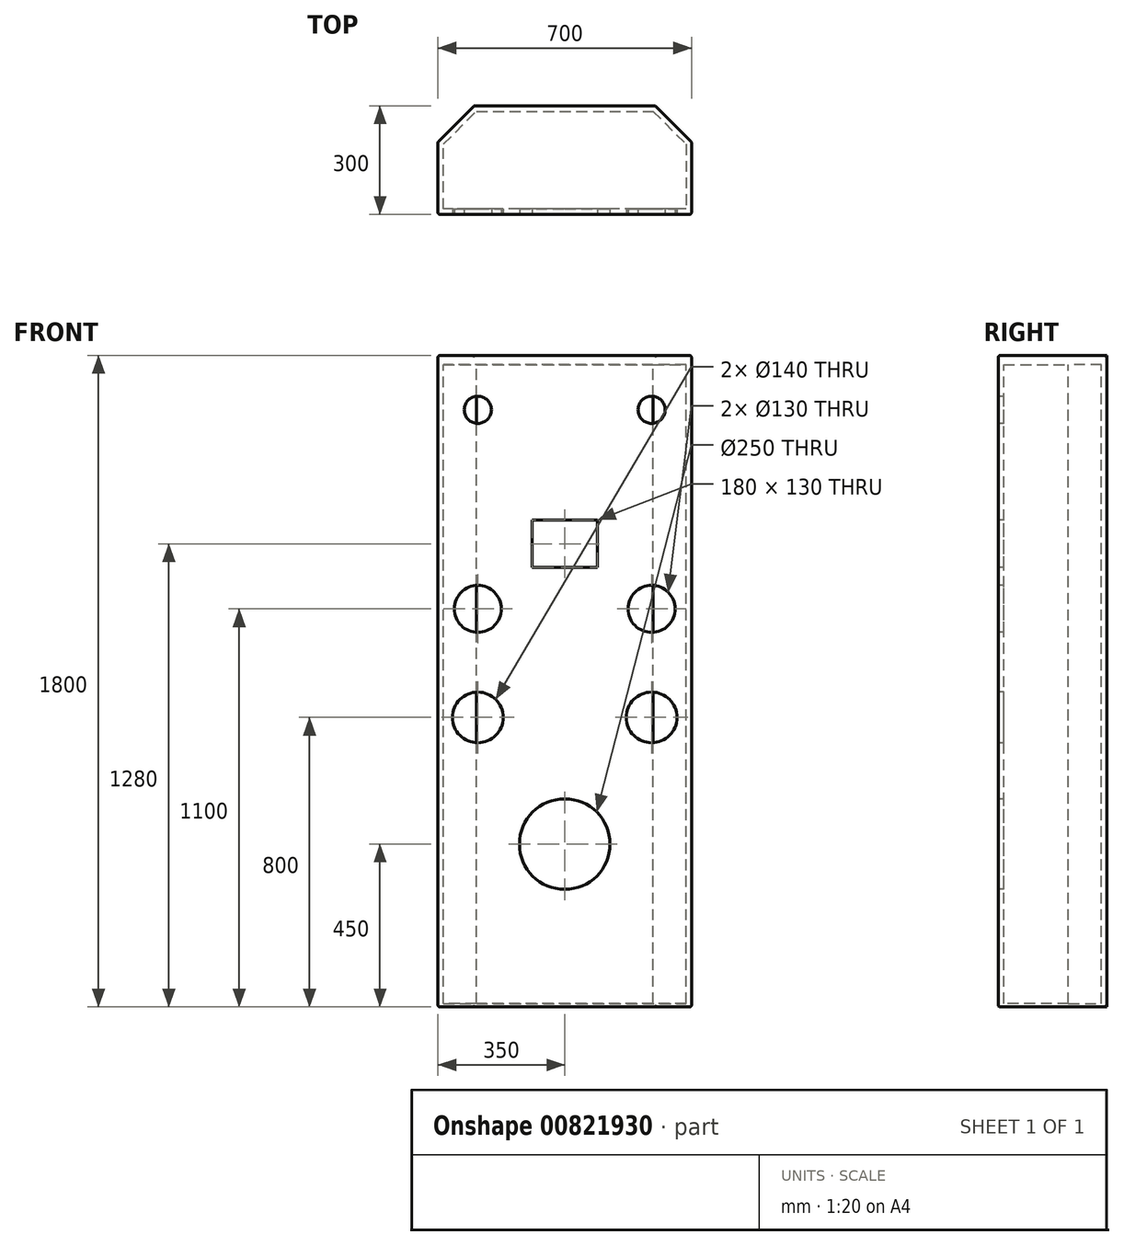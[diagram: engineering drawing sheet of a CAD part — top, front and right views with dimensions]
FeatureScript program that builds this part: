
annotation { "Feature Type Name" : "Feature", "Feature Type Description" : "" }
export const myFeature = defineFeature(function(context is Context, id is Id, definition is map)
    precondition{}
    {
        {
            var Q0;
            Q0=qCreatedBy(makeId("Top.planeOp"),FACE);
            var sketch = newSketch(context, id + "F0", { "sketchPlane" : qUnion([Q0])});
            skLineSegment(sketch, "E0.bottom", {"start": v(350, -150) * mm, "end": v(-350, -150) * mm});
            skLineSegment(sketch, "E0.top", {"start": v(250, 150) * mm, "end": v(-250, 150) * mm});
            skLineSegment(sketch, "E0.left", {"start": v(350, -150) * mm, "end": v(350, 50) * mm});
            skLineSegment(sketch, "E0.right", {"start": v(-350, -150) * mm, "end": v(-350, 50) * mm});
            skPoint(sketch, "E0.middle", {"position": v(0, 0) * mm});
            skLineSegment(sketch, "E1", {"start": v(0, 150) * mm, "end": v(-250, 150) * mm});
            skLineSegment(sketch, "E2", {"start": v(-350, 50) * mm, "end": v(-250, 150) * mm});
            skLineSegment(sketch, "E3", {"start": v(0, 150) * mm, "end": v(250, 150) * mm});
            skLineSegment(sketch, "E4", {"start": v(350, 50) * mm, "end": v(250, 150) * mm});
            skPoint(sketch, "E5.orphan", {"position": v(-350, 150) * mm});
            skPoint(sketch, "E6.orphan", {"position": v(350, 150) * mm});
            skSolve(sketch);
        }
        {
            var Q0;
            Q0 = qSketchRegion(id + "F0", true);
            extrude(context, id + "F1", {"entities" : qUnion([Q0]), "depth" : 1800 * mm, "offsetDistance" : 25 * mm});
        }
        {
            var Q0;
            Q0=makeQuery(id+"F1.opExtrude","SWEPT_EDGE",EDGE,{"disambiguationData":[OSD([sQuery(id+"F0.wireOp",EDGE,"E0.bottom"),sQuery(id+"F0.wireOp",EDGE,"E0.right")])]});
            var Q1;
            Q1=makeQuery(id+"F1.opExtrude","CAP_EDGE",EDGE,{"disambiguationData":[OSD([sQuery(id+"F0.wireOp",EDGE,"E0.bottom")])],"isStart":false});
            var Q2;
            Q2=makeQuery(id+"F1.opExtrude","SWEPT_EDGE",EDGE,{"disambiguationData":[OSD([sQuery(id+"F0.wireOp",EDGE,"E0.bottom"),sQuery(id+"F0.wireOp",EDGE,"E0.left")])]});
            var Q3;
            Q3=makeQuery(id+"F1.opExtrude","CAP_EDGE",EDGE,{"disambiguationData":[OSD([sQuery(id+"F0.wireOp",EDGE,"E0.bottom")])],"isStart":true});
            var Q4;
            Q4=makeQuery(id+"F1.opExtrude","CAP_EDGE",EDGE,{"disambiguationData":[OSD([sQuery(id+"F0.wireOp",EDGE,"E0.left")])],"isStart":true});
            var Q5;
            Q5=makeQuery(id+"F1.opExtrude","CAP_EDGE",EDGE,{"disambiguationData":[OSD([sQuery(id+"F0.wireOp",EDGE,"E0.right")])],"isStart":true});
            var Q6;
            Q6=makeQuery(id+"F1.opExtrude","CAP_EDGE",EDGE,{"disambiguationData":[OSD([sQuery(id+"F0.wireOp",EDGE,"E2")])],"isStart":true});
            var Q7;
            Q7=makeQuery(id+"F1.opExtrude","CAP_EDGE",EDGE,{"disambiguationData":[OSD([sQuery(id+"F0.wireOp",EDGE,"E1"),sQuery(id+"F0.wireOp",EDGE,"E3")])],"isStart":true});
            var Q8;
            Q8=makeQuery(id+"F1.opExtrude","CAP_EDGE",EDGE,{"disambiguationData":[OSD([sQuery(id+"F0.wireOp",EDGE,"E4")])],"isStart":true});
            var Q9;
            Q9=makeQuery(id+"F1.opExtrude","SWEPT_EDGE",EDGE,{"disambiguationData":[OSD([sQuery(id+"F0.wireOp",EDGE,"E0.left"),sQuery(id+"F0.wireOp",EDGE,"E4")])]});
            var Q10;
            Q10=makeQuery(id+"F1.opExtrude","SWEPT_EDGE",EDGE,{"disambiguationData":[OSD([sQuery(id+"F0.wireOp",EDGE,"E3"),sQuery(id+"F0.wireOp",EDGE,"E4")])]});
            var Q11;
            Q11=makeQuery(id+"F1.opExtrude","CAP_EDGE",EDGE,{"disambiguationData":[OSD([sQuery(id+"F0.wireOp",EDGE,"E4")])],"isStart":false});
            var Q12;
            Q12=makeQuery(id+"F1.opExtrude","CAP_EDGE",EDGE,{"disambiguationData":[OSD([sQuery(id+"F0.wireOp",EDGE,"E1"),sQuery(id+"F0.wireOp",EDGE,"E3")])],"isStart":false});
            var Q13;
            Q13=makeQuery(id+"F1.opExtrude","CAP_EDGE",EDGE,{"disambiguationData":[OSD([sQuery(id+"F0.wireOp",EDGE,"E0.left")])],"isStart":false});
            var Q14;
            Q14=makeQuery(id+"F1.opExtrude","CAP_EDGE",EDGE,{"disambiguationData":[OSD([sQuery(id+"F0.wireOp",EDGE,"E2")])],"isStart":false});
            var Q15;
            Q15=makeQuery(id+"F1.opExtrude","CAP_EDGE",EDGE,{"disambiguationData":[OSD([sQuery(id+"F0.wireOp",EDGE,"E0.right")])],"isStart":false});
            var Q16;
            Q16=makeQuery(id+"F1.opExtrude","SWEPT_EDGE",EDGE,{"disambiguationData":[OSD([sQuery(id+"F0.wireOp",EDGE,"E0.right"),sQuery(id+"F0.wireOp",EDGE,"E2")])]});
            var Q17;
            Q17=makeQuery(id+"F1.opExtrude","SWEPT_EDGE",EDGE,{"disambiguationData":[OSD([sQuery(id+"F0.wireOp",EDGE,"E1"),sQuery(id+"F0.wireOp",EDGE,"E2")])]});
            fillet(context, id + "F2", {"entities" : qUnion([Q0, Q1, Q2, Q3, Q4, Q5, Q6, Q7, Q8, Q9, Q10, Q11, Q12, Q13, Q14, Q15, Q16, Q17]), "radius" : 5 * mm, "tangentPropagation" : true, "allowEdgeOverflow" : false});
        }
        {
            var Q0;
            Q0=makeQuery(id+"F1.opExtrude","SWEPT_FACE",FACE,{"disambiguationData":[OSD([sQuery(id+"F0.wireOp",EDGE,"E0.bottom")])]});
            var sketch = newSketch(context, id + "F3", { "sketchPlane" : qUnion([Q0])});
            skLineSegment(sketch, "E7.bottom", {"start": v(-90, 1345) * mm, "end": v(90, 1345) * mm});
            skLineSegment(sketch, "E7.top", {"start": v(-90, 1215) * mm, "end": v(90, 1215) * mm});
            skLineSegment(sketch, "E7.left", {"start": v(-90, 1345) * mm, "end": v(-90, 1215) * mm});
            skLineSegment(sketch, "E7.right", {"start": v(90, 1345) * mm, "end": v(90, 1215) * mm});
            skLineSegment(sketch, "E8", {"start": v(0, 1795) * mm, "end": v(0, 5) * mm});
            skSolve(sketch);
        }
        {
            var Q0;
            Q0 = qSketchRegion(id + "F3", true);
            extrude(context, id + "F4", {"entities" : qUnion([Q0]), "operationType" : NewBodyOperationType.REMOVE, "oppositeDirection" : true, "depth" : 25 * mm, "offsetDistance" : 25 * mm});
        }
        {
            var Q0;
            Q0=makeQuery(id+"F1.opExtrude","CAP_FACE",FACE,{"disambiguationData":[OSD([sQuery(id+"F0.wireOp",EDGE,"E0.bottom"),sQuery(id+"F0.wireOp",EDGE,"E0.right"),sQuery(id+"F0.wireOp",EDGE,"E1"),sQuery(id+"F0.wireOp",EDGE,"E2"),sQuery(id+"F0.wireOp",EDGE,"E3"),sQuery(id+"F0.wireOp",EDGE,"E0.left"),sQuery(id+"F0.wireOp",EDGE,"E4")])],"isStart":false});
            var sketch = newSketch(context, id + "F5", { "sketchPlane" : qUnion([Q0])});
            skLineSegment(sketch, "E9.0", {"start": v(247.93, 145) * mm, "end": v(-247.93, 145) * mm});
            skLineSegment(sketch, "E10.0", {"start": v(243.79, 135) * mm, "end": v(-243.79, 135) * mm});
            skLineSegment(sketch, "E11.0", {"start": v(-243.79, 135) * mm, "end": v(-335, 43.79) * mm});
            skLineSegment(sketch, "E12.0", {"start": v(350, 50) * mm, "end": v(250, 150) * mm});
            skLineSegment(sketch, "E12.1", {"start": v(-250, 150) * mm, "end": v(-350, 50) * mm});
            skLineSegment(sketch, "E12.2", {"start": v(-350, 50) * mm, "end": v(-350, -150) * mm});
            skLineSegment(sketch, "E12.3", {"start": v(250, 150) * mm, "end": v(-250, 150) * mm});
            skLineSegment(sketch, "E12.4", {"start": v(-350, -150) * mm, "end": v(350, -150) * mm});
            skLineSegment(sketch, "E12.5", {"start": v(350, -150) * mm, "end": v(350, 50) * mm});
            skLineSegment(sketch, "E13.0", {"start": v(-335, 43.79) * mm, "end": v(-335, -135) * mm});
            skLineSegment(sketch, "E14.0", {"start": v(348.54, 51.46) * mm, "end": v(251.46, 148.54) * mm});
            skLineSegment(sketch, "E15.0", {"start": v(335, 43.79) * mm, "end": v(243.79, 135) * mm});
            skLineSegment(sketch, "E16.0", {"start": v(335, -135) * mm, "end": v(335, 43.79) * mm});
            skLineSegment(sketch, "E17.0", {"start": v(-335, -135) * mm, "end": v(335, -135) * mm});
            skSolve(sketch);
        }
        {
            var Q0;
            Q0=makeQuery(id+"F5.imprint","IMPRINT",FACE,{"disambiguationData":[TD([[makeQuery(id+"F5.imprint","IMPRINT",EDGE,{"derivedFrom":sQuery(id+"F5.wireOp",EDGE,"E10.0")}),1.0]])]});
            extrude(context, id + "F6", {"entities" : qUnion([Q0]), "operationType" : NewBodyOperationType.REMOVE, "oppositeDirection" : true, "depth" : 1790 * mm, "offsetDistance" : 25 * mm});
        }
        {
            var Q0;
            Q0=makeQuery(id+"F1.opExtrude","SWEPT_FACE",FACE,{"disambiguationData":[OSD([sQuery(id+"F0.wireOp",EDGE,"E0.bottom")])]});
            var sketch = newSketch(context, id + "F7", { "sketchPlane" : qUnion([Q0])});
            skCircle(sketch, "E18", {"center": v(240, 1650) * mm, "radius": 37.5 * mm});
            skCircle(sketch, "E19", {"center": v(240, 1100) * mm, "radius": 65 * mm});
            skLineSegment(sketch, "E20", {"start": v(0, 1795) * mm, "end": v(0, 5) * mm});
            skCircle(sketch, "E21", {"center": v(240, 800) * mm, "radius": 70 * mm});
            skCircle(sketch, "E22", {"center": v(0, 450) * mm, "radius": 125 * mm});
            skCircle(sketch, "E23.MirrorC", {"center": v(-240, 1650) * mm, "radius": 37.5 * mm});
            skCircle(sketch, "E24.MirrorC", {"center": v(-240, 1100) * mm, "radius": 65 * mm});
            skCircle(sketch, "E25.MirrorC", {"center": v(-240, 800) * mm, "radius": 70 * mm});
            skSolve(sketch);
        }
        {
            var Q0;
            Q0 = qSketchRegion(id + "F7", true);
            extrude(context, id + "F8", {"entities" : qUnion([Q0]), "operationType" : NewBodyOperationType.REMOVE, "endBound" : BoundingType.UP_TO_NEXT, "oppositeDirection" : true, "depth" : 25 * mm, "offsetDistance" : 25 * mm});
        }
        {
            var Q0;
            Q0=qCreatedBy(makeId("Top.planeOp"),FACE);
            var sketch = newSketch(context, id + "F9", { "sketchPlane" : qUnion([Q0])});
            skLineSegment(sketch, "E26.0", {"start": v(245.86, 140) * mm, "end": v(-245.86, 140) * mm});
            skLineSegment(sketch, "E26.1", {"start": v(-340, 45.86) * mm, "end": v(-340, -140) * mm});
            skLineSegment(sketch, "E26.2", {"start": v(-340, -140) * mm, "end": v(340, -140) * mm});
            skLineSegment(sketch, "E26.3", {"start": v(-245.86, 140) * mm, "end": v(-340, 45.86) * mm});
            skLineSegment(sketch, "E26.4", {"start": v(340, -140) * mm, "end": v(340, 45.86) * mm});
            skLineSegment(sketch, "E26.5", {"start": v(340, 45.86) * mm, "end": v(245.86, 140) * mm});
            skSolve(sketch);
        }
        {
            var Q0;
            Q0 = qSketchRegion(id + "F9", true);
            extrude(context, id + "F10", {"entities" : qUnion([Q0]), "operationType" : NewBodyOperationType.ADD, "depth" : 1800 * mm, "offsetDistance" : 25 * mm, "hasSecondDirection" : true, "secondDirectionOppositeDirection" : false, "secondDirectionDepth" : 1775 * mm});
        }
    });
